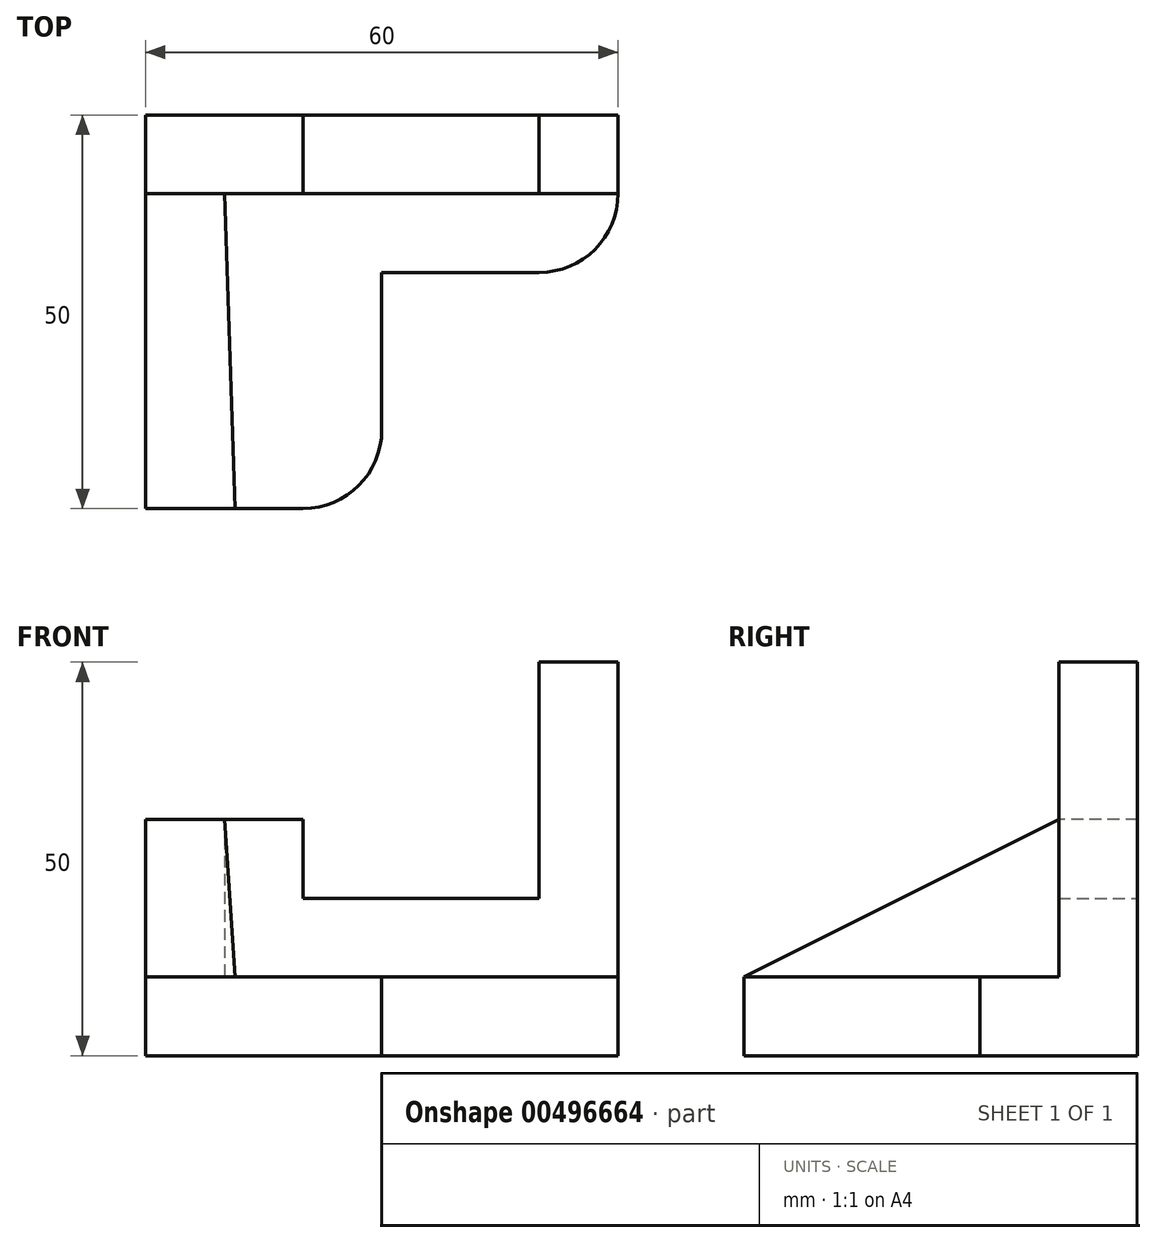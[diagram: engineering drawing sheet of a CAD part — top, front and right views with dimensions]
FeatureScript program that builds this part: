
annotation { "Feature Type Name" : "Feature", "Feature Type Description" : "" }
export const myFeature = defineFeature(function(context is Context, id is Id, definition is map)
    precondition{}
    {
        {
            var Q0;
            Q0=qCreatedBy(makeId("Top.planeOp"),FACE);
            var sketch = newSketch(context, id + "F0", { "sketchPlane" : qUnion([Q0])});
            skLineSegment(sketch, "E0", {"start": v(0, 0) * mm, "end": v(0, -50) * mm});
            skLineSegment(sketch, "E1", {"start": v(0, 0) * mm, "end": v(60, 0) * mm});
            skLineSegment(sketch, "E2", {"start": v(60, 0) * mm, "end": v(60, -20) * mm});
            skLineSegment(sketch, "E3", {"start": v(60, -20) * mm, "end": v(30, -20) * mm});
            skLineSegment(sketch, "E4", {"start": v(30, -20) * mm, "end": v(30, -50) * mm});
            skLineSegment(sketch, "E5", {"start": v(30, -50) * mm, "end": v(0, -50) * mm});
            skSolve(sketch);
        }
        {
            var Q0;
            Q0 = qSketchRegion(id + "F0", true);
            extrude(context, id + "F1", {"entities" : qUnion([Q0]), "depth" : 10 * mm});
        }
        {
            var Q0;
            Q0=makeQuery(id+"F1.opExtrude","SWEPT_EDGE",EDGE,{"disambiguationData":[OSD([sQuery(id+"F0.wireOp",EDGE,"E4"),sQuery(id+"F0.wireOp",EDGE,"E5")])]});
            var Q1;
            Q1=makeQuery(id+"F1.opExtrude","SWEPT_EDGE",EDGE,{"disambiguationData":[OSD([sQuery(id+"F0.wireOp",EDGE,"E2"),sQuery(id+"F0.wireOp",EDGE,"E3")])]});
            fillet(context, id + "F2", {"entities" : qUnion([Q0, Q1]), "radius" : 10 * mm, "tangentPropagation" : true, "allowEdgeOverflow" : false});
        }
        {
            var Q0;
            Q0=makeQuery(id+"F1.opExtrude","CAP_FACE",FACE,{"disambiguationData":[OSD([sQuery(id+"F0.wireOp",EDGE,"E0"),sQuery(id+"F0.wireOp",EDGE,"E1"),sQuery(id+"F0.wireOp",EDGE,"E2"),sQuery(id+"F0.wireOp",EDGE,"E3"),sQuery(id+"F0.wireOp",EDGE,"E4"),sQuery(id+"F0.wireOp",EDGE,"E5")])],"isStart":false});
            var sketch = newSketch(context, id + "F3", { "sketchPlane" : qUnion([Q0])});
            skLineSegment(sketch, "E6", {"start": v(60, -10) * mm, "end": v(50, -10) * mm});
            skLineSegment(sketch, "E7", {"start": v(50, -10) * mm, "end": v(50, 0) * mm});
            skLineSegment(sketch, "E8", {"start": v(50, 0) * mm, "end": v(60, 0) * mm});
            skLineSegment(sketch, "E9", {"start": v(60, 0) * mm, "end": v(60, -10) * mm});
            skSolve(sketch);
        }
        {
            var Q0;
            Q0 = qSketchRegion(id + "F3", true);
            extrude(context, id + "F4", {"entities" : qUnion([Q0]), "operationType" : NewBodyOperationType.ADD, "depth" : 40 * mm});
        }
        {
            var Q0;
            Q0=makeQuery(id+"F1.opExtrude","CAP_FACE",FACE,{"disambiguationData":[OSD([sQuery(id+"F0.wireOp",EDGE,"E0"),sQuery(id+"F0.wireOp",EDGE,"E1"),sQuery(id+"F0.wireOp",EDGE,"E2"),sQuery(id+"F0.wireOp",EDGE,"E3"),sQuery(id+"F0.wireOp",EDGE,"E4"),sQuery(id+"F0.wireOp",EDGE,"E5")])],"isStart":false});
            var sketch = newSketch(context, id + "F5", { "sketchPlane" : qUnion([Q0])});
            skLineSegment(sketch, "E10", {"start": v(50, -10) * mm, "end": v(20, -10) * mm});
            skLineSegment(sketch, "E11", {"start": v(20, -10) * mm, "end": v(20, 0) * mm});
            skLineSegment(sketch, "E12", {"start": v(20, 0) * mm, "end": v(50, 0) * mm});
            skLineSegment(sketch, "E13", {"start": v(50, 0) * mm, "end": v(50, -10) * mm});
            skSolve(sketch);
        }
        {
            var Q0;
            Q0 = qSketchRegion(id + "F5", true);
            extrude(context, id + "F6", {"entities" : qUnion([Q0]), "operationType" : NewBodyOperationType.ADD, "depth" : 10 * mm});
        }
        {
            var Q0;
            Q0=makeQuery(id+"F1.opExtrude","CAP_FACE",FACE,{"disambiguationData":[OSD([sQuery(id+"F0.wireOp",EDGE,"E0"),sQuery(id+"F0.wireOp",EDGE,"E1"),sQuery(id+"F0.wireOp",EDGE,"E2"),sQuery(id+"F0.wireOp",EDGE,"E3"),sQuery(id+"F0.wireOp",EDGE,"E4"),sQuery(id+"F0.wireOp",EDGE,"E5")])],"isStart":false});
            var sketch = newSketch(context, id + "F7", { "sketchPlane" : qUnion([Q0])});
            skLineSegment(sketch, "E14", {"start": v(20, 0) * mm, "end": v(0, 0) * mm});
            skLineSegment(sketch, "E15", {"start": v(0, 0) * mm, "end": v(0, -10) * mm});
            skLineSegment(sketch, "E16", {"start": v(0, -10) * mm, "end": v(20, -10) * mm});
            skLineSegment(sketch, "E17", {"start": v(20, -10) * mm, "end": v(20, 0) * mm});
            skSolve(sketch);
        }
        {
            var Q0;
            Q0 = qSketchRegion(id + "F7", true);
            extrude(context, id + "F8", {"entities" : qUnion([Q0]), "operationType" : NewBodyOperationType.ADD, "depth" : 20 * mm});
        }
        {
            var Q0;
            Q0=makeQuery(id+"F1.opExtrude","CAP_FACE",FACE,{"disambiguationData":[OSD([sQuery(id+"F0.wireOp",EDGE,"E0"),sQuery(id+"F0.wireOp",EDGE,"E1"),sQuery(id+"F0.wireOp",EDGE,"E2"),sQuery(id+"F0.wireOp",EDGE,"E3"),sQuery(id+"F0.wireOp",EDGE,"E4"),sQuery(id+"F0.wireOp",EDGE,"E5")])],"isStart":false});
            var sketch = newSketch(context, id + "F9", { "sketchPlane" : qUnion([Q0])});
            skLineSegment(sketch, "E18", {"start": v(0, -10) * mm, "end": v(10, -10) * mm});
            skLineSegment(sketch, "E19", {"start": v(10, -10) * mm, "end": v(11.39, -50) * mm});
            skLineSegment(sketch, "E20", {"start": v(11.39, -50) * mm, "end": v(0, -50) * mm});
            skLineSegment(sketch, "E21", {"start": v(0, -50) * mm, "end": v(0, -10) * mm});
            skSolve(sketch);
        }
        {
            var Q0;
            Q0 = qSketchRegion(id + "F9", true);
            extrude(context, id + "F10", {"entities" : qUnion([Q0]), "operationType" : NewBodyOperationType.ADD, "depth" : 20 * mm});
        }
        {
            var Q0;
            Q0=makeQuery(id+"F10.opExtrude","CAP_EDGE",EDGE,{"disambiguationData":[OSD([sQuery(id+"F9.wireOp",EDGE,"E20")])],"isStart":false});
            chamfer(context, id + "F11", {"entities" : qUnion([Q0]), "chamferType" : ChamferType.TWO_OFFSETS, "width1" : 20 * mm, "oppositeDirection" : false, "width2" : 40 * mm, "tangentPropagation" : true});
        }
    });
